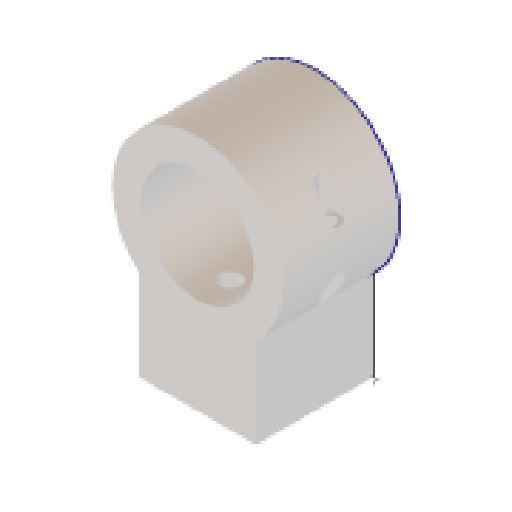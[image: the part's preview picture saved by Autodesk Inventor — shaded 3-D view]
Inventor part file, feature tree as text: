
AUTODESK INVENTOR PART (.ipt)
format: ipt  version: 2023 (Build 270158000, 158)  size: 238,592 bytes
history: native  units: mm
features: other x7, extrude x5, sketch x2, split x1, hole x1, imported_body x1
ambient origin geometry x8: Origin, YZ Plane, XZ Plane, XY Plane, X Axis, Y Axis, Z Axis, Center Point
bodies: Solid1 (feature_tree)
feature tree (17):
  extrude  "Extrusion1"  Depth=85.0mm
  other  "BoltPlane"
  other  "BoltHoles"
  extrude  "Extrusion2"  Depth=62.0mm
  extrude  "Extrusion3"  Depth=62.0mm TaperAngle=0.0deg
  other  "NutPlane"
  other  "NutHoles"
  extrude  "Extrusion4"  Depth=62.0mm
  other  "SplitPlane"
  split  "Split2"
  hole  "Hole2"  [1 undecoded]
  sketch  "Sketch4"  dims[d2=75.866mm d3=29.0mm d4=58.0mm d5=0.0mm d6=50.0mm d7=6.0mm d8=6.4mm d9=10.4mm d10=58.0mm d11=0.0mm d12=40.0mm d13=0.0mm d14=-80.0mm d15=10.4mm d16=70.0mm d17=0.0mm d18=0.0mm d28=12.5mm d29=6.2mm d30=6.0mm d31=4.0mm d32=2.0mm d33=90.0deg d34=8.0mm d35=0.0mm d36=10.2mm d37=10.2mm d38=18.0mm d39=62.0mm d40=0.0mm]
  other  "BoltHeadLevel"
  extrude  "Extrusion5"  Depth=62.0mm
  sketch  "Sketch1"  dims[d0=55.9mm d1=85.0mm]
  other  "UPPER"
  imported_body  "BASE"
note: 1 required parameter value undecoded (feature->parameter linkage not recoverable at this tier; creation-order binding heuristic only, values carry confidence <= 0.55)
